# Revit family: KS ALU-PU 80 -s-, DS 40, M16, Ø219,1
name_source: partatom
category: HLS-Bauteile
revit_build: Autodesk Revit 2017 (Build: 20190507_1515(x64)
units: mm (PartAtom-declared; Revit-internal decimal feet)

## family parameters
Arbeitsebenenbasiert = Ja
Beim Laden mit Abzugskörper schneiden = Nein
Bemaßung runder Anschluss = Durchmesser verwenden
Gemeinsam genutzt = Ja
Immer vertikal = Nein
Raumberechnungspunkt = Nein
Teiletyp = Normal

## types (1)
- Kälteschelle ALU-PU 80 -s-, DS 40, M16, Ø219,1
    A = 64 mm
    AB = 1 mm  [stored 0.00328084 ft]
    Anschluss = M16
    Anschlußhöhe = 65 mm
    Artikelnummer = 7622195
    B = 376 mm  [stored 1.2336 ft]
    Baustoffklasse = B2
    Breite = 380 mm
    D = 219 mm
    D0 = 299 mm
    DF1 = 34 mm
    DF2 = 34 mm
    DS = 40 mm  [stored 0.131234 ft]
    DVS = 18 mm
    Dichte Kern = 80 kg/m³
    Dichte Mantel = 2.700 kg/m³
    Dicke Mantel = 0,08 mm
    Dmax = 220 mm
    Dmin = 218 mm
    Dämmkörper = ALU/PU
    Dämmstärke = 40 mm  [stored 0.131234 ft]
    EAN = 4250928444851
    Fabrikat = MEFA
    Firma = MEFA Befestigungs- und Montagesysteme GmbH
    Gewicht = 1.60 kg
    Gewicht pro Bauteil = 1.60 kg
    H = 327 mm
    HGA = 20 mm  [stored 0.0656168 ft]
    Kurztext1 = Kälteschelle RG80s ALU/PU
    Kurztext2 = 219,1 mm Iso 40 x 100 mm M16
    L = 100 mm  [stored 0.328084 ft]
    MB = 35 mm  [stored 0.114829 ft]
    MD = 4 mm  [stored 0.0131234 ft]
    Material = Stahl
    Material Mantel = Alufolie
    Materialname = S235
    Mengeneinheit = St
    Oberflaeche = galvanisch verzinkt
    R = 150 mm
    RM = 154 mm
    Rohraußendurchmesser Stahl = 219,1 mm
    Rohrschellentyp = Maxima PSM
    S = 342 mm  [stored 1.12205 ft]
    Schalenlänge = 100 mm
    Vorgabe-Ansicht = 1219 mm
    Wasserdampfdiffusionswiderstand = 18750 µ
    Wärmeleitfähigkeit = 0.025 W/mK
    max. Temperaturbeständigkeit = 120 °C
    max. zul. Last = 2.20 kN
    mittl. Nenndruckfestigkeit Kern = 0,5 N/mm²
    stat. Belastung Kern = 0,1 N/mm²
    vpe = 1 St

note: [stored X ft] marks values corroborated as IEEE doubles in the binary element streams (Revit-internal decimal feet)

## geometry (parser evidence)
native form markers: Sweep x6
no freeform markers — native parametric forms only
